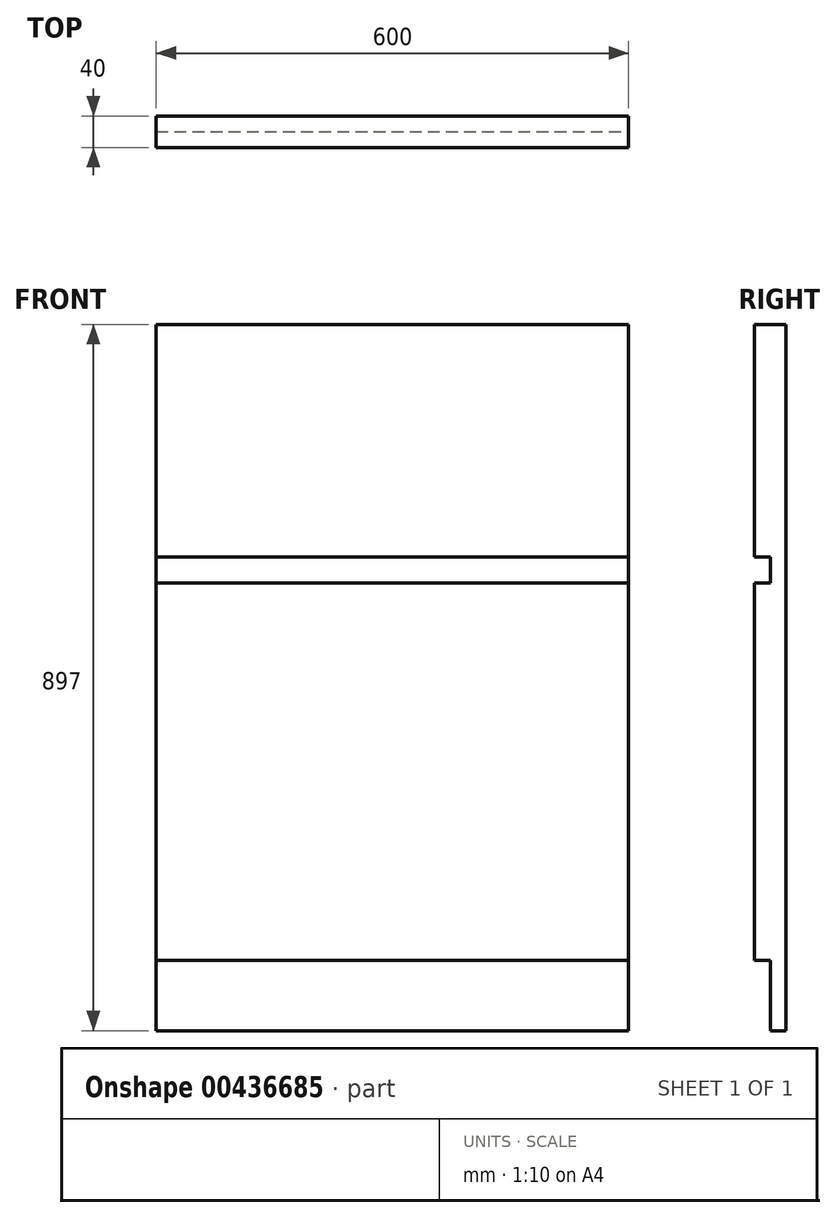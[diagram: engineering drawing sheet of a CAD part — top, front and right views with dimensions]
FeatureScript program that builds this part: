
annotation { "Feature Type Name" : "Feature", "Feature Type Description" : "" }
export const myFeature = defineFeature(function(context is Context, id is Id, definition is map)
    precondition{}
    {
        {
            var Q0;
            Q0=qCreatedBy(makeId("Front.planeOp"),FACE);
            var sketch = newSketch(context, id + "F0", { "sketchPlane" : qUnion([Q0])});
            skLineSegment(sketch, "E0.bottom", {"start": v(300, 448.5) * mm, "end": v(-300, 448.5) * mm});
            skLineSegment(sketch, "E0.top", {"start": v(300, -448.5) * mm, "end": v(-300, -448.5) * mm});
            skLineSegment(sketch, "E0.left", {"start": v(300, 448.5) * mm, "end": v(300, -448.5) * mm});
            skLineSegment(sketch, "E0.right", {"start": v(-300, 448.5) * mm, "end": v(-300, -448.5) * mm});
            skPoint(sketch, "E0.middle", {"position": v(0, 0) * mm});
            skSolve(sketch);
        }
        {
            var Q0;
            Q0 = qSketchRegion(id + "F0", true);
            extrude(context, id + "F1", {"entities" : qUnion([Q0]), "depth" : 20 * mm});
        }
        {
            var Q0;
            Q0=makeQuery(id+"F1.opExtrude","CAP_FACE",FACE,{"disambiguationData":[OSD([sQuery(id+"F0.wireOp",EDGE,"E0.bottom"),sQuery(id+"F0.wireOp",EDGE,"E0.top"),sQuery(id+"F0.wireOp",EDGE,"E0.left"),sQuery(id+"F0.wireOp",EDGE,"E0.right")])],"isStart":false});
            var sketch = newSketch(context, id + "F2", { "sketchPlane" : qUnion([Q0])});
            skLineSegment(sketch, "E1.bottom", {"start": v(-300, 448.5) * mm, "end": v(300, 448.5) * mm});
            skLineSegment(sketch, "E1.top", {"start": v(-300, 153.5) * mm, "end": v(300, 153.5) * mm});
            skLineSegment(sketch, "E1.left", {"start": v(-300, 448.5) * mm, "end": v(-300, 153.5) * mm});
            skLineSegment(sketch, "E1.right", {"start": v(300, 448.5) * mm, "end": v(300, 153.5) * mm});
            skLineSegment(sketch, "E2.bottom", {"start": v(-300, -359.5) * mm, "end": v(300, -359.5) * mm});
            skLineSegment(sketch, "E2.top", {"start": v(-300, 120.5) * mm, "end": v(300, 120.5) * mm});
            skLineSegment(sketch, "E2.left", {"start": v(-300, -359.5) * mm, "end": v(-300, 120.5) * mm});
            skLineSegment(sketch, "E2.right", {"start": v(300, -359.5) * mm, "end": v(300, 120.5) * mm});
            skSolve(sketch);
        }
        {
            var Q0;
            Q0 = qSketchRegion(id + "F2", true);
            var Q1;
            {var subQ1=sQuery(id+"F2.wireOp",EDGE,"E2.bottom");Q1=makeQuery(id+"F2.imprint","IMPRINT",FACE,{"disambiguationData":[TD([[makeQuery(id+"F2.imprint","IMPRINT",EDGE,{"derivedFrom":subQ1}),1.0]])]});}
            extrude(context, id + "F3", {"entities" : qUnion([Q0, Q1]), "operationType" : NewBodyOperationType.ADD, "depth" : 20 * mm});
        }
    });
